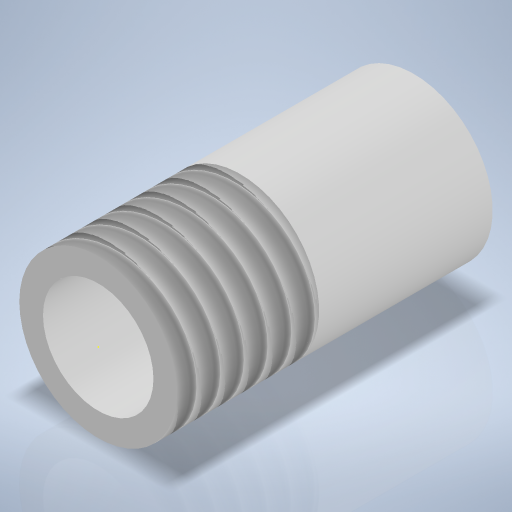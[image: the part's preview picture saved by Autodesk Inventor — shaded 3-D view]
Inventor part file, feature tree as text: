
AUTODESK INVENTOR PART (.ipt)
format: ipt  version: 2024 (Build 280153000, 153)  size: 264,192 bytes
history: native  units: mm
features: sketch x2, extrude x1, thread x1
ambient origin geometry x8: Origin, YZ Plane, XZ Plane, XY Plane, X Axis, Y Axis, Z Axis, Center Point
bodies: Volumenkörper1 (feature_tree)
feature tree (4):
  sketch  "Skizze1"  dims[d0=10.0mm d1=7.0mm d2=20.0mm d3=0.0mm]
  extrude  "Extrusion1"  Depth=20.0mm
  thread  "Gewinde1"  [1 undecoded]
  sketch  "Skizze2"  dims[d4=9.0mm d5=0.0mm]
note: 1 required parameter value undecoded (feature->parameter linkage not recoverable at this tier; creation-order binding heuristic only, values carry confidence <= 0.55)
